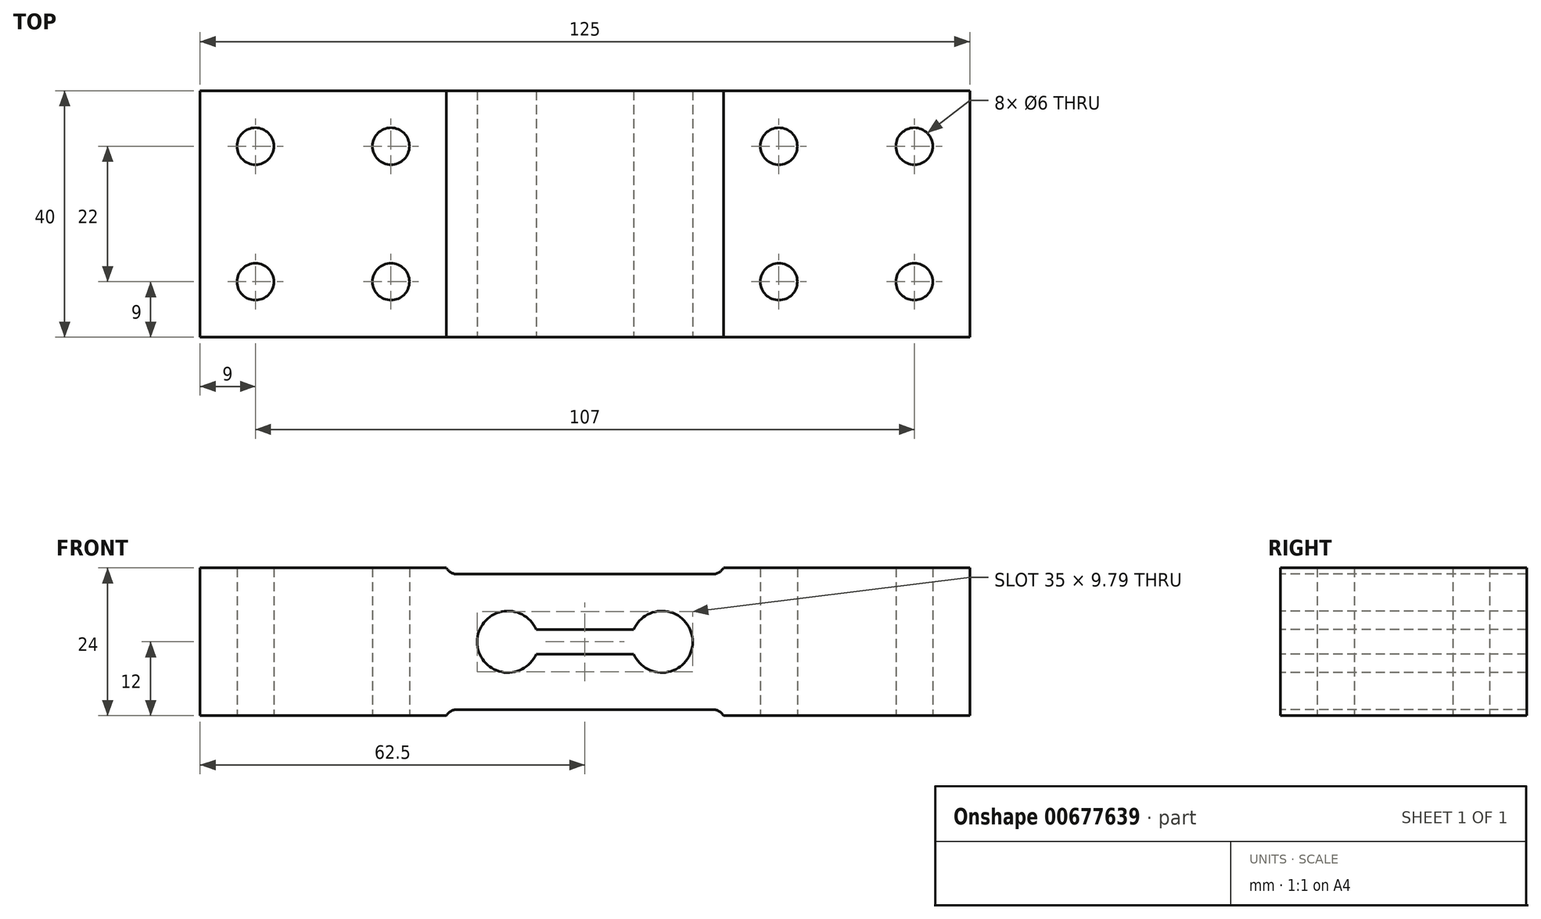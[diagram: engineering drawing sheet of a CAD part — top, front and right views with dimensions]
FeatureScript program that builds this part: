
annotation { "Feature Type Name" : "Feature", "Feature Type Description" : "" }
export const myFeature = defineFeature(function(context is Context, id is Id, definition is map)
    precondition{}
    {
        {
            var Q0;
            Q0=qCreatedBy(makeId("Top.planeOp"),FACE);
            var sketch = newSketch(context, id + "F0", { "sketchPlane" : qUnion([Q0])});
            skLineSegment(sketch, "E0.bottom", {"start": v(0, 0) * mm, "end": v(125, 0) * mm});
            skLineSegment(sketch, "E0.top", {"start": v(0, 40) * mm, "end": v(125, 40) * mm});
            skLineSegment(sketch, "E0.left", {"start": v(0, 0) * mm, "end": v(0, 40) * mm});
            skLineSegment(sketch, "E0.right", {"start": v(125, 0) * mm, "end": v(125, 40) * mm});
            skCircle(sketch, "E1", {"center": v(116, 9) * mm, "radius": 3 * mm});
            skCircle(sketch, "E2.0.1.0", {"center": v(116, 31) * mm, "radius": 3 * mm});
            skCircle(sketch, "E2.1.0.0", {"center": v(94, 9) * mm, "radius": 3 * mm});
            skCircle(sketch, "E2.1.1.0", {"center": v(94, 31) * mm, "radius": 3 * mm});
            skLineSegment(sketch, "E2.direction1", {"start": v(116, 9) * mm, "end": v(94, 9) * mm, "construction": true});
            skLineSegment(sketch, "E2.direction2", {"start": v(116, 9) * mm, "end": v(116, 31) * mm, "construction": true});
            skCircle(sketch, "E3", {"center": v(9, 9) * mm, "radius": 3 * mm});
            skCircle(sketch, "E4.0.1.0", {"center": v(9, 31) * mm, "radius": 3 * mm});
            skCircle(sketch, "E4.1.0.0", {"center": v(31, 9) * mm, "radius": 3 * mm});
            skCircle(sketch, "E4.1.1.0", {"center": v(31, 31) * mm, "radius": 3 * mm});
            skLineSegment(sketch, "E4.direction1", {"start": v(9, 9) * mm, "end": v(31, 9) * mm, "construction": true});
            skLineSegment(sketch, "E4.direction2", {"start": v(9, 9) * mm, "end": v(9, 31) * mm, "construction": true});
            skSolve(sketch);
        }
        {
            var Q0;
            Q0=makeQuery(id+"F0.imprint","IMPRINT",FACE,{"disambiguationData":[TD([[makeQuery(id+"F0.imprint","IMPRINT",EDGE,{"derivedFrom":sQuery(id+"F0.wireOp",EDGE,"E0.bottom")}),1.0]])]});
            extrude(context, id + "F1", {"entities" : qUnion([Q0]), "depth" : 24 * mm, "offsetDistance" : 25 * mm});
        }
        {
            var Q0;
            Q0=makeQuery(id+"F1.opExtrude","SWEPT_FACE",FACE,{"disambiguationData":[OSD([sQuery(id+"F0.wireOp",EDGE,"E0.bottom")])]});
            var sketch = newSketch(context, id + "F2", { "sketchPlane" : qUnion([Q0])});
            skCircle(sketch, "E5", {"center": v(50, 12) * mm, "radius": 5 * mm});
            skCircle(sketch, "E6", {"center": v(75, 12) * mm, "radius": 5 * mm});
            skLineSegment(sketch, "E7.bottom", {"start": v(54, 14) * mm, "end": v(71, 14) * mm});
            skLineSegment(sketch, "E7.top", {"start": v(54, 10) * mm, "end": v(71, 10) * mm});
            skLineSegment(sketch, "E7.left", {"start": v(54, 14) * mm, "end": v(54, 10) * mm});
            skLineSegment(sketch, "E7.right", {"start": v(71, 14) * mm, "end": v(71, 10) * mm});
            skSolve(sketch);
        }
        {
            var Q0;
            {var subQ5=sQuery(id+"F2.wireOp",EDGE,"E7.left");Q0=makeQuery(id+"F2.imprint","IMPRINT",FACE,{"disambiguationData":[TD([[makeQuery(id+"F2.imprint","IMPRINT",EDGE,{"derivedFrom":subQ5}),-1.0]])]});}
            var Q1;
            {var subQ5=sQuery(id+"F2.wireOp",EDGE,"E7.left");Q1=makeQuery(id+"F2.imprint","IMPRINT",FACE,{"disambiguationData":[TD([[makeQuery(id+"F2.imprint","IMPRINT",EDGE,{"derivedFrom":subQ5}),1.0]])]});}
            var Q2;
            {var subQ0=sQuery(id+"F2.wireOp",EDGE,"E7.bottom");var subQ1=sQuery(id+"F2.wireOp",EDGE,"E5");var subQ2=makeQuery(id+"F2.imprint","INTERSECT",VERTEX,{"derivedFrom":[subQ1,subQ0]});Q2=makeQuery(id+"F2.imprint","IMPRINT",FACE,{"disambiguationData":[TD([[makeQuery(id+"F2.imprint","IMPRINT",EDGE,{"disambiguationData":[TD([[subQ2,1.0]])],"derivedFrom":subQ1}),-1.0]])]});}
            var Q3;
            {var subQ5=sQuery(id+"F2.wireOp",EDGE,"E7.right");Q3=makeQuery(id+"F2.imprint","IMPRINT",FACE,{"disambiguationData":[TD([[makeQuery(id+"F2.imprint","IMPRINT",EDGE,{"derivedFrom":subQ5}),-1.0]])]});}
            var Q4;
            {var subQ5=sQuery(id+"F2.wireOp",EDGE,"E7.right");Q4=makeQuery(id+"F2.imprint","IMPRINT",FACE,{"disambiguationData":[TD([[makeQuery(id+"F2.imprint","IMPRINT",EDGE,{"derivedFrom":subQ5}),1.0]])]});}
            extrude(context, id + "F3", {"entities" : qUnion([Q0, Q1, Q2, Q3, Q4]), "operationType" : NewBodyOperationType.REMOVE, "oppositeDirection" : true, "depth" : 45 * mm, "offsetDistance" : 25 * mm});
        }
        {
            var Q0;
            Q0=makeQuery(id+"F1.opExtrude","CAP_FACE",FACE,{"disambiguationData":[OSD([sQuery(id+"F0.wireOp",EDGE,"E0.bottom"),sQuery(id+"F0.wireOp",EDGE,"E0.top"),sQuery(id+"F0.wireOp",EDGE,"E0.left"),sQuery(id+"F0.wireOp",EDGE,"E0.right"),sQuery(id+"F0.wireOp",EDGE,"E1"),sQuery(id+"F0.wireOp",EDGE,"E2.0.1.0"),sQuery(id+"F0.wireOp",EDGE,"E2.1.0.0"),sQuery(id+"F0.wireOp",EDGE,"E2.1.1.0"),sQuery(id+"F0.wireOp",EDGE,"E3"),sQuery(id+"F0.wireOp",EDGE,"E4.0.1.0"),sQuery(id+"F0.wireOp",EDGE,"E4.1.0.0"),sQuery(id+"F0.wireOp",EDGE,"E4.1.1.0")])],"isStart":false});
            var sketch = newSketch(context, id + "F4", { "sketchPlane" : qUnion([Q0])});
            skLineSegment(sketch, "E8.bottom", {"start": v(40, 40) * mm, "end": v(85, 40) * mm});
            skLineSegment(sketch, "E8.top", {"start": v(40, 0) * mm, "end": v(85, 0) * mm});
            skLineSegment(sketch, "E8.left", {"start": v(40, 40) * mm, "end": v(40, 0) * mm});
            skLineSegment(sketch, "E8.right", {"start": v(85, 40) * mm, "end": v(85, 0) * mm});
            skSolve(sketch);
        }
        {
            var Q0;
            Q0=makeQuery(id+"F4.imprint","IMPRINT",FACE,{"disambiguationData":[TD([[makeQuery(id+"F4.imprint","IMPRINT",EDGE,{"derivedFrom":sQuery(id+"F4.wireOp",EDGE,"E8.bottom")}),-1.0]])]});
            extrude(context, id + "F5", {"entities" : qUnion([Q0]), "operationType" : NewBodyOperationType.REMOVE, "oppositeDirection" : true, "depth" : 1 * mm, "offsetDistance" : 25 * mm});
        }
        {
            var Q0;
            Q0=makeQuery(id+"F1.opExtrude","CAP_FACE",FACE,{"disambiguationData":[OSD([sQuery(id+"F0.wireOp",EDGE,"E0.bottom"),sQuery(id+"F0.wireOp",EDGE,"E0.top"),sQuery(id+"F0.wireOp",EDGE,"E0.left"),sQuery(id+"F0.wireOp",EDGE,"E0.right"),sQuery(id+"F0.wireOp",EDGE,"E1"),sQuery(id+"F0.wireOp",EDGE,"E2.0.1.0"),sQuery(id+"F0.wireOp",EDGE,"E2.1.0.0"),sQuery(id+"F0.wireOp",EDGE,"E2.1.1.0"),sQuery(id+"F0.wireOp",EDGE,"E3"),sQuery(id+"F0.wireOp",EDGE,"E4.0.1.0"),sQuery(id+"F0.wireOp",EDGE,"E4.1.0.0"),sQuery(id+"F0.wireOp",EDGE,"E4.1.1.0")])],"isStart":true});
            var sketch = newSketch(context, id + "F6", { "sketchPlane" : qUnion([Q0])});
            skLineSegment(sketch, "E9.bottom", {"start": v(40, 0) * mm, "end": v(85, 0) * mm});
            skLineSegment(sketch, "E9.top", {"start": v(40, -40) * mm, "end": v(85, -40) * mm});
            skLineSegment(sketch, "E9.left", {"start": v(40, 0) * mm, "end": v(40, -40) * mm});
            skLineSegment(sketch, "E9.right", {"start": v(85, 0) * mm, "end": v(85, -40) * mm});
            skSolve(sketch);
        }
        {
            var Q0;
            Q0=makeQuery(id+"F6.imprint","IMPRINT",FACE,{"disambiguationData":[TD([[makeQuery(id+"F6.imprint","IMPRINT",EDGE,{"derivedFrom":sQuery(id+"F6.wireOp",EDGE,"E9.bottom")}),-1.0]])]});
            extrude(context, id + "F7", {"entities" : qUnion([Q0]), "operationType" : NewBodyOperationType.REMOVE, "oppositeDirection" : true, "depth" : 1 * mm, "offsetDistance" : 25 * mm});
        }
        {
            var Q0;
            Q0=makeQuery(id+"F7.boolean.opBoolean","COPY",EDGE,{"derivedFrom":makeQuery(id+"F7.opExtrude","CAP_EDGE",EDGE,{"disambiguationData":[OSD([sQuery(id+"F6.wireOp",EDGE,"E9.left")])],"isStart":false})});
            var Q1;
            Q1=makeQuery(id+"F7.boolean.opBoolean","COPY",EDGE,{"derivedFrom":makeQuery(id+"F7.opExtrude","CAP_EDGE",EDGE,{"disambiguationData":[OSD([sQuery(id+"F6.wireOp",EDGE,"E9.right")])],"isStart":false})});
            var Q2;
            Q2=makeQuery(id+"F5.boolean.opBoolean","COPY",EDGE,{"derivedFrom":makeQuery(id+"F5.opExtrude","CAP_EDGE",EDGE,{"disambiguationData":[OSD([sQuery(id+"F4.wireOp",EDGE,"E8.right")])],"isStart":false})});
            var Q3;
            Q3=makeQuery(id+"F5.boolean.opBoolean","COPY",EDGE,{"derivedFrom":makeQuery(id+"F5.opExtrude","CAP_EDGE",EDGE,{"disambiguationData":[OSD([sQuery(id+"F4.wireOp",EDGE,"E8.left")])],"isStart":false})});
            fillet(context, id + "F8", {"entities" : qUnion([Q0, Q1, Q2, Q3]), "radius" : 2 * mm, "tangentPropagation" : true, "allowEdgeOverflow" : false});
        }
    });
